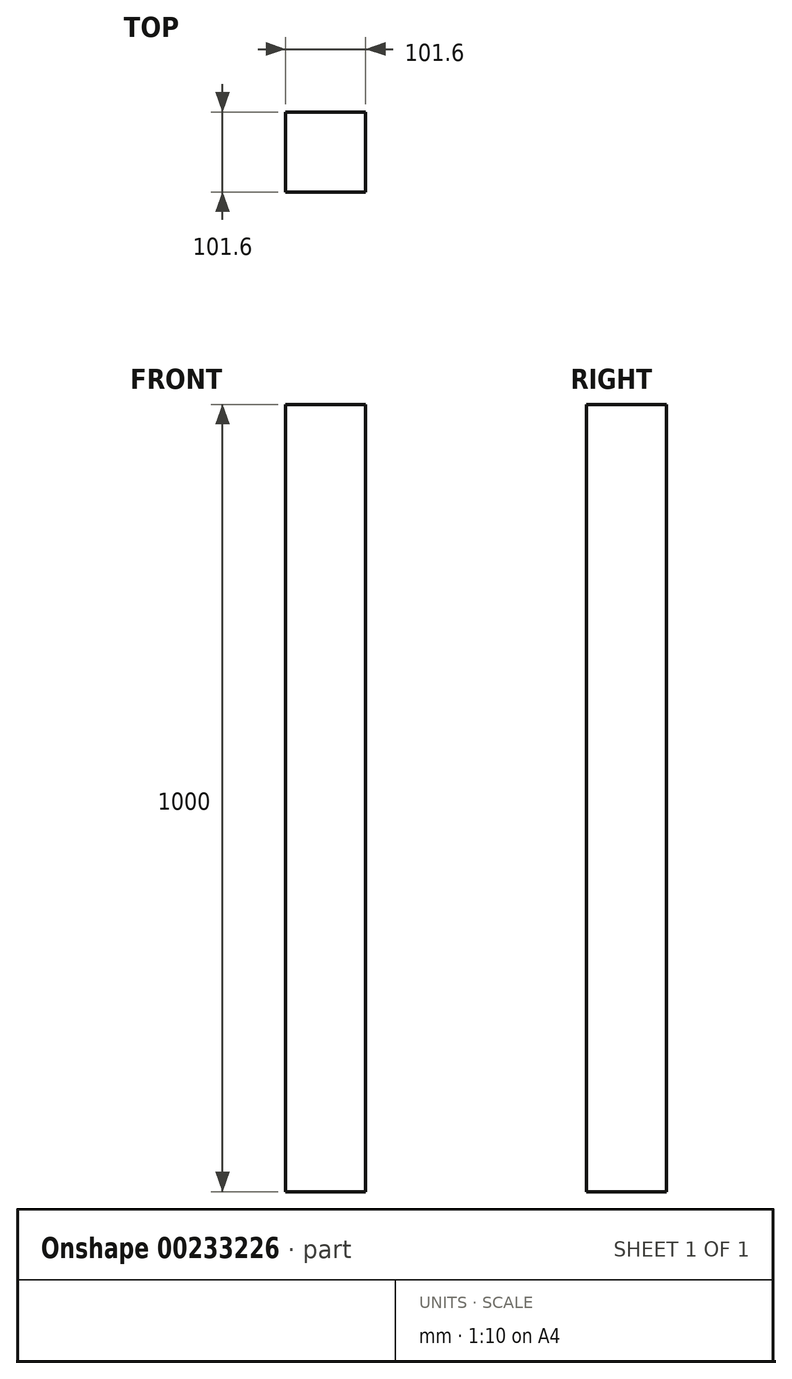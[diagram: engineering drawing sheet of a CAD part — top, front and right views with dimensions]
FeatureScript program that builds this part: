
annotation { "Feature Type Name" : "Feature", "Feature Type Description" : "" }
export const myFeature = defineFeature(function(context is Context, id is Id, definition is map)
    precondition{}
    {
        {
            var Q0;
            Q0=qCreatedBy(makeId("Front.planeOp"),FACE);
            var sketch = newSketch(context, id + "F0", { "sketchPlane" : qUnion([Q0])});
            skLineSegment(sketch, "E0.bottom", {"start": v(-426.47, 510.63) * mm, "end": v(-324.87, 510.63) * mm});
            skLineSegment(sketch, "E0.top", {"start": v(-426.47, -489.37) * mm, "end": v(-324.87, -489.37) * mm});
            skLineSegment(sketch, "E0.left", {"start": v(-426.47, 510.63) * mm, "end": v(-426.47, -489.37) * mm});
            skLineSegment(sketch, "E0.right", {"start": v(-324.87, 510.63) * mm, "end": v(-324.87, -489.37) * mm});
            skSolve(sketch);
        }
        {
            var Q0;
            Q0=qSketchRegion(id+"F0",true);
            extrude(context, id + "F1", {"entities" : qUnion([Q0]), "depth" : 101.6 * mm});
        }
    });
